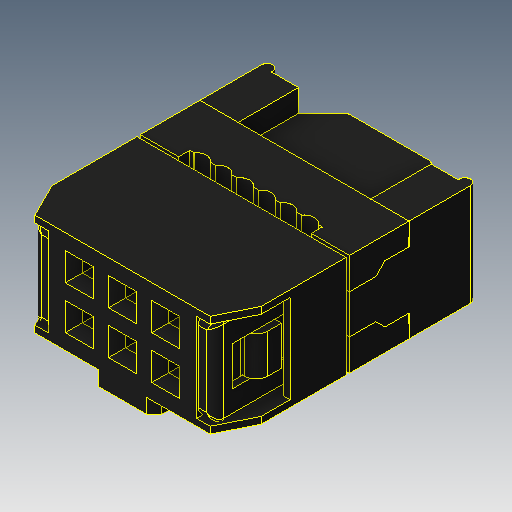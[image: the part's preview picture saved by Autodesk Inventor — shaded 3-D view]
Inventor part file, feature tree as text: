
AUTODESK INVENTOR PART (.ipt)
format: ipt  version: 2018 (Build 220112000, 112)  size: 1,506,304 bytes
history: native  units: mm
features: other x2, sketch x1
ambient origin geometry x8: Origin, YZ Plane, XZ Plane, XY Plane, X Axis, Y Axis, Z Axis, Center Point
bodies: Body1 (feature_tree), Body2 (feature_tree), Body3 (feature_tree), Body4 (feature_tree), Body5 (feature_tree), Body6 (feature_tree), Body7 (feature_tree), Body8 (feature_tree), Body9 (feature_tree), Body10 (feature_tree), Body11 (feature_tree), Body12 (feature_tree), Body13 (feature_tree), Body14 (feature_tree), Body15 (feature_tree), Body16 (feature_tree), Body17 (feature_tree), Body18 (feature_tree), Body19 (feature_tree), Body20 (feature_tree), Body21 (feature_tree), Body22 (feature_tree), Body23 (feature_tree), Body24 (feature_tree), Body25 (feature_tree), Body26 (feature_tree), Body27 (feature_tree), Body28 (feature_tree), Body29 (feature_tree), Body30 (feature_tree), Body31 (feature_tree), Body32 (feature_tree), Body33 (feature_tree), Body34 (feature_tree), Body35 (feature_tree), Body36 (feature_tree), Body37 (feature_tree), Body38 (feature_tree), Body39 (feature_tree), Body40 (feature_tree), Body41 (feature_tree), Body42 (feature_tree), Body43 (feature_tree), Body44 (feature_tree), Body45 (feature_tree), Body46 (feature_tree), Body47 (feature_tree), Body48 (feature_tree), Body49 (feature_tree), Body50 (feature_tree), Body51 (feature_tree), Body52 (feature_tree), Body53 (feature_tree), Body54 (feature_tree), Body55 (feature_tree), Body56 (feature_tree), Body57 (feature_tree), Body58 (feature_tree), Body59 (feature_tree), Body60 (feature_tree), Body61 (feature_tree), Body62 (feature_tree), Body63 (feature_tree), Body64 (feature_tree), Body65 (feature_tree), Body66 (feature_tree), Body67 (feature_tree), Body68 (feature_tree), Body69 (feature_tree), Body70 (feature_tree), Body71 (feature_tree), Body72 (feature_tree), Body73 (feature_tree), Body74 (feature_tree), Body75 (feature_tree), Body76 (feature_tree), Body77 (feature_tree), Body78 (feature_tree), Body79 (feature_tree), Body80 (feature_tree), Body81 (feature_tree), Body82 (feature_tree), Body83 (feature_tree), Body84 (feature_tree), Body85 (feature_tree), Body86 (feature_tree), Body87 (feature_tree), Body88 (feature_tree), Body89 (feature_tree), Body90 (feature_tree), Body91 (feature_tree), Body92 (feature_tree), Body93 (feature_tree), Body94 (feature_tree), Body95 (feature_tree), Body96 (feature_tree), Body97 (feature_tree), Body98 (feature_tree), Body99 (feature_tree), Body100 (feature_tree), Body101 (feature_tree), Body102 (feature_tree), Body103 (feature_tree), Body104 (feature_tree), Body105 (feature_tree), Body106 (feature_tree), Body107 (feature_tree), Body108 (feature_tree), Body109 (feature_tree), Body110 (feature_tree), Body111 (feature_tree), Body112 (feature_tree), Body113 (feature_tree), Body114 (feature_tree), Body115 (feature_tree), Body116 (feature_tree), Body117 (feature_tree), Body118 (feature_tree), Body119 (feature_tree), Body120 (feature_tree), Body121 (feature_tree), Body122 (feature_tree), Body123 (feature_tree), Body124 (feature_tree), Body125 (feature_tree), Body126 (feature_tree), Body127 (feature_tree), Body128 (feature_tree), Body129 (feature_tree), Body130 (feature_tree), Body131 (feature_tree), Body132 (feature_tree), Body133 (feature_tree), Body134 (feature_tree), Body135 (feature_tree), Body136 (feature_tree), Body137 (feature_tree), Body138 (feature_tree), Body139 (feature_tree), Body140 (feature_tree), Body141 (feature_tree), Body142 (feature_tree), Body143 (feature_tree), Body144 (feature_tree), Body145 (feature_tree), Body146 (feature_tree), Body147 (feature_tree), Body148 (feature_tree), Body149 (feature_tree), Body150 (feature_tree), Body151 (feature_tree), Body152 (feature_tree), Body153 (feature_tree), Body154 (feature_tree), Body155 (feature_tree), Body156 (feature_tree), Body157 (feature_tree), Body158 (feature_tree), Body159 (feature_tree), Body160 (feature_tree), Body161 (feature_tree), Body162 (feature_tree), Body163 (feature_tree), Body164 (feature_tree), Body165 (feature_tree), Body166 (feature_tree), Body167 (feature_tree), Body168 (feature_tree), Body169 (feature_tree), Body170 (feature_tree), Body171 (feature_tree), Body172 (feature_tree), Body173 (feature_tree), Body174 (feature_tree), Body175 (feature_tree), Body176 (feature_tree), Body177 (feature_tree), Body178 (feature_tree), Body179 (feature_tree), Body180 (feature_tree), Body181 (feature_tree), Body182 (feature_tree), Body183 (feature_tree), Body184 (feature_tree), Body185 (feature_tree), Body186 (feature_tree), Body187 (feature_tree), Body188 (feature_tree), Body189 (feature_tree), Body190 (feature_tree), Body191 (feature_tree), Body192 (feature_tree), Body193 (feature_tree), Body194 (feature_tree), Body195 (feature_tree), Body196 (feature_tree), Body197 (feature_tree), Body198 (feature_tree), Body199 (feature_tree), Body200 (feature_tree), Body201 (feature_tree), Body202 (feature_tree), Body203 (feature_tree), Body204 (feature_tree), Body205 (feature_tree), Body206 (feature_tree), Body207 (feature_tree), Body208 (feature_tree), Body209 (feature_tree), Body210 (feature_tree), Body211 (feature_tree), Body212 (feature_tree), Body213 (feature_tree), Body214 (feature_tree), Body215 (feature_tree), Body216 (feature_tree), Body217 (feature_tree), Body218 (feature_tree), Body219 (feature_tree), Body220 (feature_tree), Body221 (feature_tree), Body222 (feature_tree), Body223 (feature_tree), Body224 (feature_tree), Body225 (feature_tree), Body226 (feature_tree), Body227 (feature_tree), Body228 (feature_tree), Body229 (feature_tree), Body230 (feature_tree), Body231 (feature_tree), Body232 (feature_tree), Body233 (feature_tree), Body234 (feature_tree), Body235 (feature_tree), Body236 (feature_tree), Body237 (feature_tree), Body238 (feature_tree), Body239 (feature_tree), Body240 (feature_tree), Body241 (feature_tree), Body242 (feature_tree), Body243 (feature_tree), Body244 (feature_tree), Body245 (feature_tree), Body246 (feature_tree), Body247 (feature_tree), Body248 (feature_tree), Body249 (feature_tree), Body250 (feature_tree), Body251 (feature_tree), Body252 (feature_tree), Body253 (feature_tree), Body254 (feature_tree), Body255 (feature_tree), Body256 (feature_tree), Body257 (feature_tree), Body258 (feature_tree), Body259 (feature_tree), Body260 (feature_tree), Body261 (feature_tree), Body262 (feature_tree), Body263 (feature_tree), Body264 (feature_tree), Body265 (feature_tree), Body266 (feature_tree), Body267 (feature_tree), Body268 (feature_tree), Body269 (feature_tree), Body270 (feature_tree), Body271 (feature_tree), Body272 (feature_tree), Body273 (feature_tree), Body274 (feature_tree), Body275 (feature_tree), Body276 (feature_tree), Body277 (feature_tree), Body278 (feature_tree), Body279 (feature_tree), Body280 (feature_tree), Body281 (feature_tree), Body282 (feature_tree), Body283 (feature_tree), Body284 (feature_tree), Body285 (feature_tree), Body286 (feature_tree), Body287 (feature_tree), Body288 (feature_tree), Body289 (feature_tree), Body290 (feature_tree), Body291 (feature_tree), Body292 (feature_tree), Body293 (feature_tree), Body294 (feature_tree), Body295 (feature_tree), Body296 (feature_tree), Body297 (feature_tree), Body298 (feature_tree), Body299 (feature_tree), Body300 (feature_tree), Body301 (feature_tree), Body302 (feature_tree), Body303 (feature_tree), Body304 (feature_tree), Body305 (feature_tree), Body306 (feature_tree), Body307 (feature_tree), Body308 (feature_tree), Body309 (feature_tree), Body310 (feature_tree), Body311 (feature_tree), Body312 (feature_tree), Body313 (feature_tree), Body314 (feature_tree), Body315 (feature_tree), Body316 (feature_tree), Body317 (feature_tree), Body318 (feature_tree), Body319 (feature_tree), Body320 (feature_tree), Body321 (feature_tree), Body322 (feature_tree), Body323 (feature_tree), Body324 (feature_tree), Body325 (feature_tree), Body326 (feature_tree), Body327 (feature_tree), Body328 (feature_tree), Body329 (feature_tree), Body330 (feature_tree), Body331 (feature_tree), Body332 (feature_tree), Body333 (feature_tree), Body334 (feature_tree), Body335 (feature_tree), Body336 (feature_tree), Body337 (feature_tree), Body338 (feature_tree), Body339 (feature_tree), Body340 (feature_tree), Body341 (feature_tree), Body342 (feature_tree), Body343 (feature_tree), Body344 (feature_tree), Body345 (feature_tree), Body346 (feature_tree), Body347 (feature_tree), Body348 (feature_tree), Body349 (feature_tree), Body350 (feature_tree), Body351 (feature_tree), Body352 (feature_tree), Body353 (feature_tree), Body354 (feature_tree), Body355 (feature_tree), Body356 (feature_tree), Body357 (feature_tree), Body358 (feature_tree), Body359 (feature_tree), Body360 (feature_tree), Body361 (feature_tree), Body362 (feature_tree), Body363 (feature_tree), Body364 (feature_tree), Body365 (feature_tree), Body366 (feature_tree), Body367 (feature_tree), Body368 (feature_tree), Body369 (feature_tree), Body370 (feature_tree), Body371 (feature_tree), Body372 (feature_tree), Body373 (feature_tree), Body374 (feature_tree), Body375 (feature_tree), Body376 (feature_tree), Body377 (feature_tree), Body378 (feature_tree), Body379 (feature_tree), Body380 (feature_tree), Body381 (feature_tree), Body382 (feature_tree), Body383 (feature_tree), Body384 (feature_tree), Body385 (feature_tree), Body386 (feature_tree), Body387 (feature_tree), Body388 (feature_tree), Body389 (feature_tree), Body390 (feature_tree), Body391 (feature_tree), Body392 (feature_tree), Body393 (feature_tree), Body394 (feature_tree), Body395 (feature_tree), Body396 (feature_tree), Body397 (feature_tree), Body398 (feature_tree), Body399 (feature_tree), Body400 (feature_tree), Body401 (feature_tree), Body402 (feature_tree), Body403 (feature_tree), Body404 (feature_tree), Body405 (feature_tree), Body406 (feature_tree), Body407 (feature_tree), Body408 (feature_tree), Body409 (feature_tree), Body410 (feature_tree), Body411 (feature_tree), Body412 (feature_tree), Body413 (feature_tree), Body414 (feature_tree), Body415 (feature_tree), Body416 (feature_tree), Body417 (feature_tree), Body418 (feature_tree), Body419 (feature_tree), Body420 (feature_tree), Body421 (feature_tree), Body422 (feature_tree), Body423 (feature_tree), Body424 (feature_tree), Body425 (feature_tree), Body426 (feature_tree), Body427 (feature_tree), Body428 (feature_tree), Body429 (feature_tree), Body430 (feature_tree), Body431 (feature_tree), Body432 (feature_tree), Body433 (feature_tree), Body434 (feature_tree), Body435 (feature_tree), Body436 (feature_tree), Body437 (feature_tree), Body438 (feature_tree), Body439 (feature_tree), Body440 (feature_tree), Body441 (feature_tree), Body442 (feature_tree), Body443 (feature_tree), Body444 (feature_tree), Body445 (feature_tree), Body446 (feature_tree), Body447 (feature_tree), Body448 (feature_tree), Body449 (feature_tree), Body450 (feature_tree), Body451 (feature_tree), Body452 (feature_tree), Body453 (feature_tree), Body454 (feature_tree), Body455 (feature_tree), Body456 (feature_tree), Body457 (feature_tree), Body458 (feature_tree), Body459 (feature_tree), Body460 (feature_tree), Body461 (feature_tree), Body462 (feature_tree), Body463 (feature_tree), Body464 (feature_tree), Body465 (feature_tree), Body466 (feature_tree), Body467 (feature_tree), Body468 (feature_tree), Body469 (feature_tree), Body470 (feature_tree), Body471 (feature_tree), Body472 (feature_tree), Body473 (feature_tree), Body474 (feature_tree), Body475 (feature_tree), Body476 (feature_tree), Body477 (feature_tree), Body478 (feature_tree), Body479 (feature_tree), Body480 (feature_tree), Body481 (feature_tree), Body482 (feature_tree), Body483 (feature_tree), Body484 (feature_tree), Body485 (feature_tree), Body486 (feature_tree), Body487 (feature_tree), Body488 (feature_tree), Body489 (feature_tree), Body490 (feature_tree), Body491 (feature_tree), Body492 (feature_tree), Body493 (feature_tree), Body494 (feature_tree), Body495 (feature_tree), Body496 (feature_tree), Body497 (feature_tree), Body498 (feature_tree), Body499 (feature_tree), Body500 (feature_tree), Body501 (feature_tree), Body502 (feature_tree), Body503 (feature_tree), Body504 (feature_tree), Body505 (feature_tree), Body506 (feature_tree), Body507 (feature_tree), Body508 (feature_tree), Body509 (feature_tree), Body510 (feature_tree), Body511 (feature_tree), Body512 (feature_tree), Body513 (feature_tree), Body514 (feature_tree), Body515 (feature_tree), Body516 (feature_tree), Body517 (feature_tree), Body518 (feature_tree), Body519 (feature_tree), Body520 (feature_tree), Body521 (feature_tree), Body522 (feature_tree), Body523 (feature_tree), Body524 (feature_tree), Body525 (feature_tree), Body526 (feature_tree), Body527 (feature_tree), Body528 (feature_tree), Body529 (feature_tree), Body530 (feature_tree), Body531 (feature_tree), Body532 (feature_tree), Body533 (feature_tree), Body534 (feature_tree), Body535 (feature_tree), Body536 (feature_tree), Body537 (feature_tree), Body538 (feature_tree), Body539 (feature_tree), Body540 (feature_tree), Body541 (feature_tree), Body542 (feature_tree), Body543 (feature_tree), Body544 (feature_tree), Body545 (feature_tree), Body546 (feature_tree)
feature tree (3):
  sketch  "Sketch1"  dims[d0=0.5mm d1=0.05mm]
  other  "Composite1"
  other  "Srf1"
